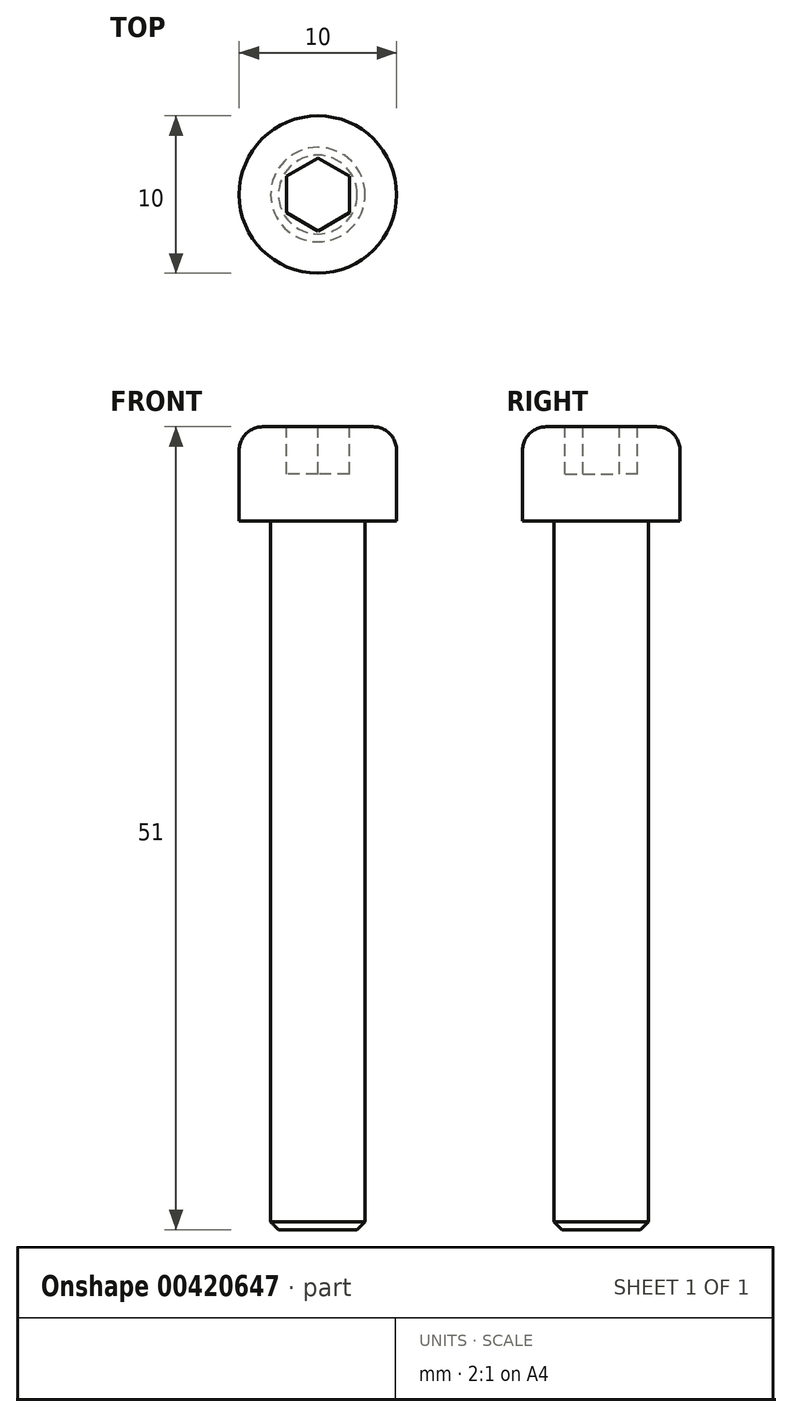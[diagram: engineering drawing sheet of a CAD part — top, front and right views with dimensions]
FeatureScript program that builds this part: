
annotation { "Feature Type Name" : "Feature", "Feature Type Description" : "" }
export const myFeature = defineFeature(function(context is Context, id is Id, definition is map)
    precondition{}
    {
        {
            var Q0;
            Q0=qCreatedBy(makeId("Front.planeOp"),FACE);
            var sketch = newSketch(context, id + "F0", { "sketchPlane" : qUnion([Q0])});
            skLineSegment(sketch, "E0", {"start": v(0, 0) * mm, "end": v(0, 58.1) * mm, "construction": true});
            skLineSegment(sketch, "E1", {"start": v(0, 0) * mm, "end": v(-3, 0) * mm});
            skLineSegment(sketch, "E2", {"start": v(-3, 0) * mm, "end": v(-3, 45) * mm});
            skLineSegment(sketch, "E3", {"start": v(-3, 45) * mm, "end": v(-5, 45) * mm});
            skLineSegment(sketch, "E4", {"start": v(-5, 45) * mm, "end": v(-5, 51) * mm});
            skLineSegment(sketch, "E5", {"start": v(-5, 51) * mm, "end": v(0, 51) * mm});
            skLineSegment(sketch, "E6", {"start": v(0, 51) * mm, "end": v(0, 0) * mm});
            skSolve(sketch);
        }
        {
            var Q0;
            Q0=makeQuery(id+"F0.imprint","IMPRINT",FACE,{"disambiguationData":[TD([[makeQuery(id+"F0.imprint","IMPRINT",EDGE,{"derivedFrom":sQuery(id+"F0.wireOp",EDGE,"E1")}),-1.0]])]});
            var Q1;
            Q1=sQuery(id+"F0.wireOp",EDGE,"E0");
            revolve(context, id + "F1", {"entities" : qUnion([Q0]), "axis" : qUnion([Q1]), "revolveType" : RevolveType.FULL});
        }
        {
            var Q0;
            Q0=makeQuery(id+"F1.opRevolve","SWEPT_EDGE",EDGE,{"disambiguationData":[OSD([sQuery(id+"F0.wireOp",EDGE,"E1"),sQuery(id+"F0.wireOp",EDGE,"E2")])]});
            chamfer(context, id + "F2", {"entities" : qUnion([Q0]), "width" : 0.5 * mm, "tangentPropagation" : true});
        }
        {
            var Q0;
            Q0=makeQuery(id+"F1.opRevolve","SWEPT_EDGE",EDGE,{"disambiguationData":[OSD([sQuery(id+"F0.wireOp",EDGE,"E4"),sQuery(id+"F0.wireOp",EDGE,"E5")])]});
            fillet(context, id + "F3", {"entities" : qUnion([Q0]), "radius" : 1.5 * mm, "tangentPropagation" : true, "allowEdgeOverflow" : false});
        }
        {
            var Q0;
            Q0=makeQuery(id+"F1.opRevolve","SWEPT_FACE",FACE,{"disambiguationData":[OSD([sQuery(id+"F0.wireOp",EDGE,"E5")])]});
            var sketch = newSketch(context, id + "F4", { "sketchPlane" : qUnion([Q0])});
            skCircle(sketch, "E7.cCircle", {"center": v(0, 0) * mm, "radius": 2 * mm, "construction": true});
            skLineSegment(sketch, "E7.0", {"start": v(-2, -1.15) * mm, "end": v(-2, 1.15) * mm});
            skLineSegment(sketch, "E7.1", {"start": v(-2, 1.15) * mm, "end": v(0, 2.3) * mm});
            skLineSegment(sketch, "E7.2", {"start": v(0, 2.3) * mm, "end": v(2, 1.15) * mm});
            skLineSegment(sketch, "E7.3", {"start": v(2, 1.15) * mm, "end": v(2, -1.15) * mm});
            skLineSegment(sketch, "E7.4", {"start": v(2, -1.15) * mm, "end": v(0, -2.3) * mm});
            skLineSegment(sketch, "E7.5", {"start": v(0, -2.3) * mm, "end": v(-2, -1.15) * mm});
            skPoint(sketch, "E7.0.midPoint", {"position": v(-2, 0) * mm});
            skSolve(sketch);
        }
        {
            var Q0;
            Q0=qSketchRegion(id+"F4",true);
            extrude(context, id + "F5", {"entities" : qUnion([Q0]), "operationType" : NewBodyOperationType.REMOVE, "oppositeDirection" : true, "depth" : 3 * mm});
        }
    });
